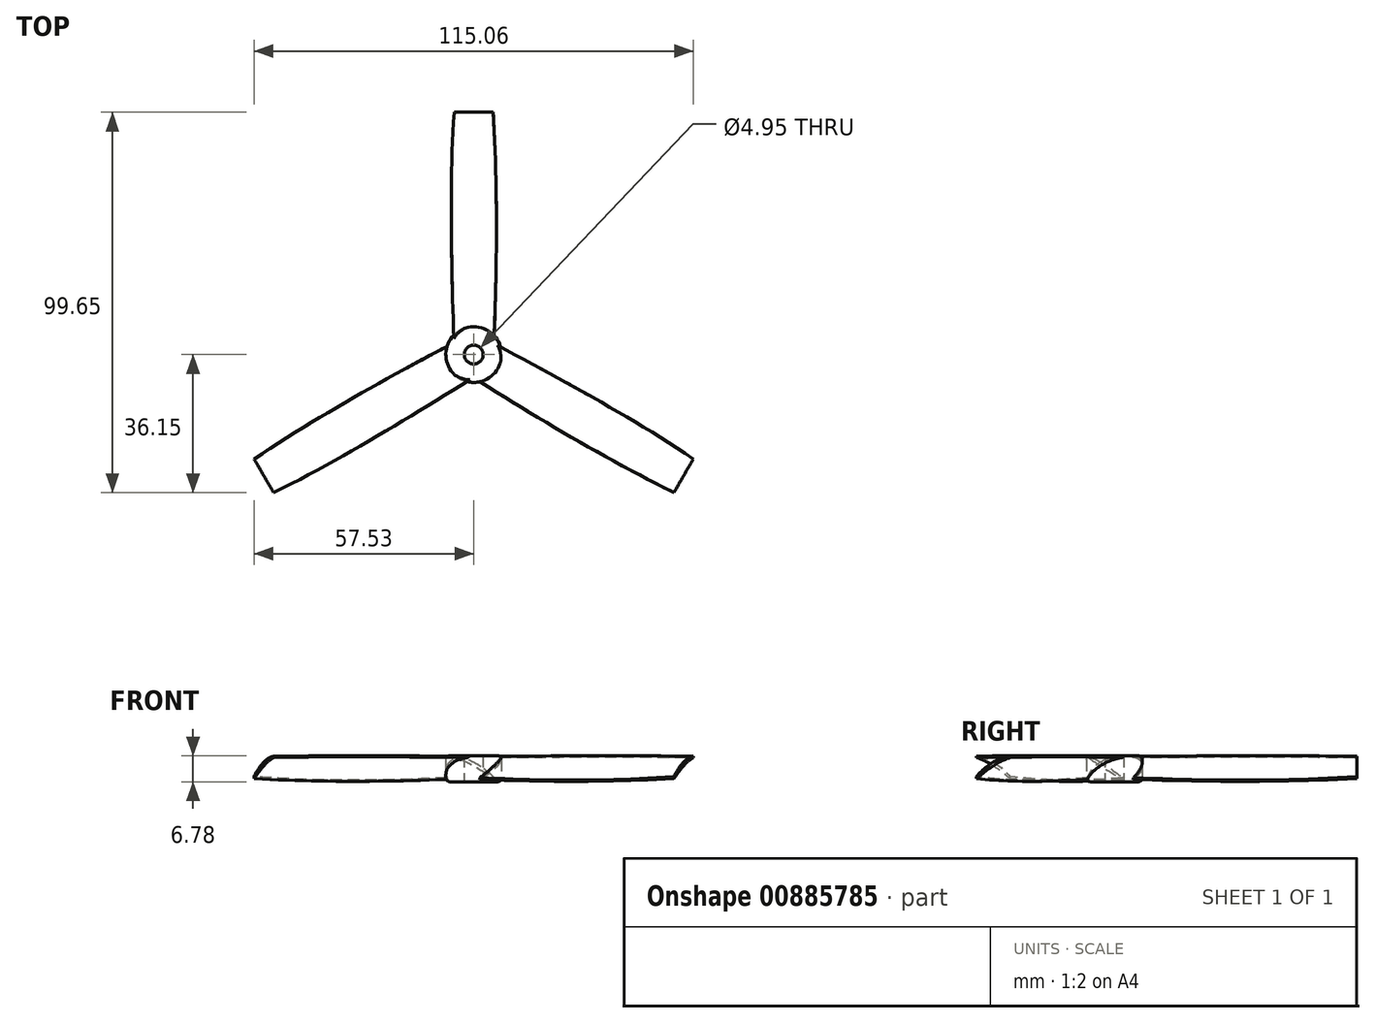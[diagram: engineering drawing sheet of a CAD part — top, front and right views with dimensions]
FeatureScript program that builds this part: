
annotation { "Feature Type Name" : "Feature", "Feature Type Description" : "" }
export const myFeature = defineFeature(function(context is Context, id is Id, definition is map)
    precondition{}
    {
        {
            var Q0;
            Q0=qCreatedBy(makeId("Top.planeOp"),FACE);
            var sketch = newSketch(context, id + "F0", { "sketchPlane" : qUnion([Q0])});
            skCircle(sketch, "E0", {"center": v(0, 0) * mm, "radius": 2.48 * mm});
            skCircle(sketch, "E1", {"center": v(0, 0) * mm, "radius": 7.3 * mm});
            skSolve(sketch);
        }
        {
            var Q0;
            Q0 = qSketchRegion(id + "F0", true);
            extrude(context, id + "F1", {"entities" : qUnion([Q0]), "depth" : 6.78 * mm, "offsetDistance" : 25.4 * mm});
        }
        {
            var Q0;
            Q0=qCreatedBy(makeId("Top.planeOp"),FACE);
            var sketch = newSketch(context, id + "F2", { "sketchPlane" : qUnion([Q0])});
            skLineSegment(sketch, "E2", {"start": v(0, 0) * mm, "end": v(0, 63.5) * mm, "construction": true});
            skLineSegment(sketch, "E3", {"start": v(0, 63.5) * mm, "end": v(6.1, 63.5) * mm, "construction": true});
            skLineSegment(sketch, "E4", {"start": v(0, 63.5) * mm, "end": v(-6.1, 63.5) * mm, "construction": true});
            skLineSegment(sketch, "E5.bottom", {"start": v(-6.1, 63.5) * mm, "end": v(6.1, 63.5) * mm});
            skLineSegment(sketch, "E5.top", {"start": v(-6.1, 2.67) * mm, "end": v(6.1, 2.67) * mm});
            skLineSegment(sketch, "E5.left", {"start": v(-6.1, 63.5) * mm, "end": v(-6.1, 2.67) * mm});
            skLineSegment(sketch, "E5.right", {"start": v(6.1, 63.5) * mm, "end": v(6.1, 2.67) * mm});
            skSolve(sketch);
        }
        {
            var Q0;
            Q0 = qSketchRegion(id + "F2", true);
            extrude(context, id + "F3", {"entities" : qUnion([Q0]), "operationType" : NewBodyOperationType.ADD, "depth" : 6.78 * mm, "offsetDistance" : 25.4 * mm});
        }
        {
            var Q0;
            Q0=makeQuery(id+"F3.opExtrude","SWEPT_FACE",FACE,{"disambiguationData":[OSD([sQuery(id+"F2.wireOp",EDGE,"E5.bottom")])]});
            var sketch = newSketch(context, id + "F4", { "sketchPlane" : qUnion([Q0])});
            skFitSpline(sketch, "E6", {"points": [v(6.1, 6.78) * mm, v(-6.1, 0.27) * mm], "startDerivative": vector(-15.33, -1.1) * mm, "endDerivative": vector(-10.35, -11.38) * mm});
            skFitSpline(sketch, "E7", {"points": [v(6.1, 6.55) * mm, v(-6.1, 0) * mm], "startDerivative": vector(-10.21, -1.69) * mm, "endDerivative": vector(-12.76, -10.4) * mm});
            skLineSegment(sketch, "E8", {"start": v(6.1, 6.78) * mm, "end": v(6.1, 6.55) * mm});
            skLineSegment(sketch, "E9", {"start": v(-6.1, 0.27) * mm, "end": v(-6.1, 0) * mm});
            skSolve(sketch);
        }
        {
            var Q0;
            Q0=makeQuery(id+"F4.imprint","IMPRINT",FACE,{"disambiguationData":[TD([[makeQuery(id+"F4.imprint","IMPRINT",EDGE,{"derivedFrom":sQuery(id+"F4.wireOp",EDGE,"E6")}),1.0]])]});
            extrude(context, id + "F5", {"entities" : qUnion([Q0]), "operationType" : NewBodyOperationType.INTERSECT, "oppositeDirection" : true, "depth" : 59.69 * mm, "offsetDistance" : 25.4 * mm});
        }
        {
            var Q0;
            Q0=qCreatedBy(makeId("Top.planeOp"),FACE);
            var sketch = newSketch(context, id + "F6", { "sketchPlane" : qUnion([Q0])});
            skLineSegment(sketch, "E10", {"start": v(0, 0) * mm, "end": v(0, 63.5) * mm, "construction": true});
            skLineSegment(sketch, "E11", {"start": v(0, 63.5) * mm, "end": v(-5.08, 63.5) * mm, "construction": true});
            skLineSegment(sketch, "E12", {"start": v(0, 63.5) * mm, "end": v(5.08, 63.5) * mm, "construction": true});
            skFitSpline(sketch, "E13", {"points": [v(-5.08, 63.5) * mm, v(-5.08, 0) * mm], "startDerivative": vector(-4.39, -54.25) * mm, "endDerivative": vector(1.96, -63.67) * mm});
            skFitSpline(sketch, "E14", {"points": [v(5.08, 63.5) * mm, v(5.08, 0) * mm], "startDerivative": vector(3.8, -59.51) * mm, "endDerivative": vector(-3.2, -59.02) * mm});
            skLineSegment(sketch, "E15", {"start": v(-5.08, 63.5) * mm, "end": v(5.08, 63.5) * mm});
            skLineSegment(sketch, "E16", {"start": v(-5.08, 0) * mm, "end": v(5.08, 0) * mm});
            skSolve(sketch);
        }
        {
            var Q0;
            Q0 = qSketchRegion(id + "F6", true);
            extrude(context, id + "F7", {"entities" : qUnion([Q0]), "operationType" : NewBodyOperationType.INTERSECT, "depth" : 25.4 * mm, "offsetDistance" : 25.4 * mm});
        }
        {
            var Q0;
            Q0=makeQuery(id+"F0.imprint","IMPRINT",FACE,{"disambiguationData":[TD([[makeQuery(id+"F0.imprint","IMPRINT",EDGE,{"derivedFrom":sQuery(id+"F0.wireOp",EDGE,"E0")}),-1.0]])]});
            extrude(context, id + "F8", {"entities" : qUnion([Q0]), "operationType" : NewBodyOperationType.ADD, "depth" : 6.78 * mm, "offsetDistance" : 25.4 * mm});
        }
        {
            var Q0;
            Q0=makeQuery(id+"F1.opExtrude","SWEPT_BODY",BODY,{"disambiguationData":[OSD([sQuery(id+"F0.wireOp",EDGE,"E0"),sQuery(id+"F0.wireOp",EDGE,"E1")])]});
            var Q1;
            Q1=makeQuery(id+"F8.opExtrude","CAP_EDGE",EDGE,{"disambiguationData":[OSD([sQuery(id+"F0.wireOp",EDGE,"E0")])],"isStart":false});
            circularPattern(context, id + "F9", {"operationType" : NewBodyOperationType.ADD, "entities" : qUnion([Q0]), "axis" : qUnion([Q1]), "angle" : 360 * degree, "instanceCount" : 3, "equalSpace" : true, "isCentered" : true, "computeTransformsWithoutBuiltin" : true});
        }
        {
            var Q0;
            Q0=makeQuery(id+"F8.opExtrude","CAP_EDGE",EDGE,{"disambiguationData":[OSD([sQuery(id+"F0.wireOp",EDGE,"E1")])],"isStart":false});
            var Q1;
            Q1=makeQuery(id+"F8.opExtrude","CAP_EDGE",EDGE,{"disambiguationData":[OSD([sQuery(id+"F0.wireOp",EDGE,"E1")])],"isStart":true});
            fillet(context, id + "F10", {"entities" : qUnion([Q0, Q1]), "radius" : 1.02 * mm, "tangentPropagation" : true, "allowEdgeOverflow" : false});
        }
    });
